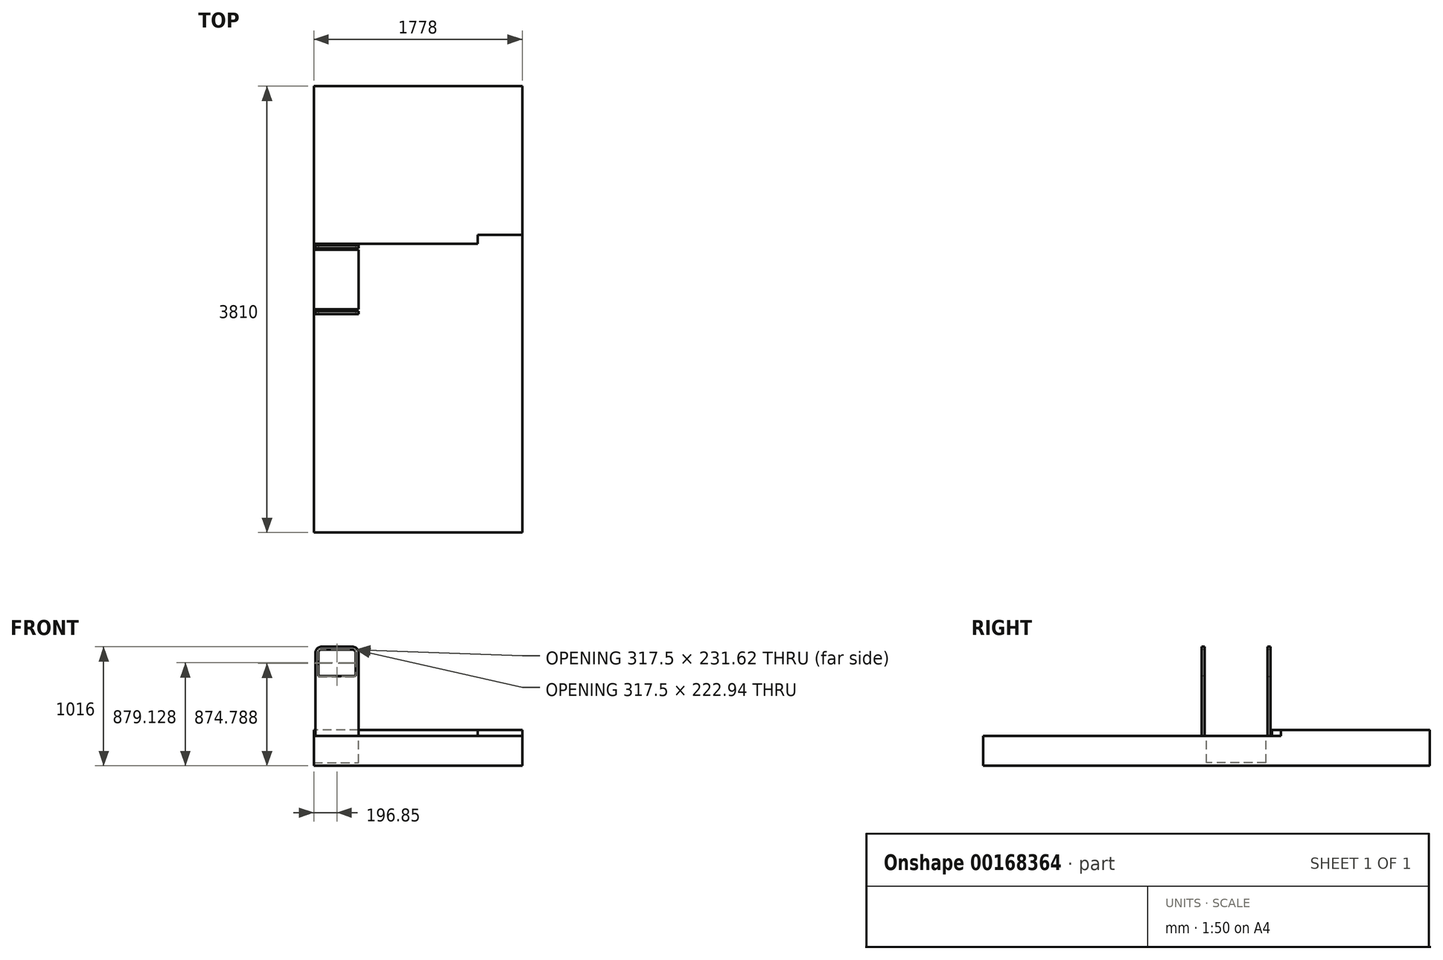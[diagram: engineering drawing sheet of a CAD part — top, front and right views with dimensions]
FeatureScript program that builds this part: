
annotation { "Feature Type Name" : "Feature", "Feature Type Description" : "" }
export const myFeature = defineFeature(function(context is Context, id is Id, definition is map)
    precondition{}
    {
        {
            var Q0;
            Q0=qCreatedBy(makeId("Top.planeOp"),FACE);
            var sketch = newSketch(context, id + "F0", { "sketchPlane" : qUnion([Q0])});
            skLineSegment(sketch, "E0.bottom", {"start": v(-889, 1905) * mm, "end": v(889, 1905) * mm});
            skLineSegment(sketch, "E0.top", {"start": v(-889, -1905) * mm, "end": v(889, -1905) * mm});
            skLineSegment(sketch, "E0.left", {"start": v(-889, 1905) * mm, "end": v(-889, -1905) * mm});
            skLineSegment(sketch, "E0.right", {"start": v(889, 1905) * mm, "end": v(889, -1905) * mm});
            skPoint(sketch, "E0.middle", {"position": v(0, 0) * mm});
            skLineSegment(sketch, "E1", {"start": v(889, 635) * mm, "end": v(508, 635) * mm});
            skLineSegment(sketch, "E2", {"start": v(508, 635) * mm, "end": v(508, 558.8) * mm});
            skLineSegment(sketch, "E3", {"start": v(508, 558.8) * mm, "end": v(-889, 558.8) * mm});
            skLineSegment(sketch, "E4", {"start": v(-889, 304.8) * mm, "end": v(-508, 304.8) * mm});
            skLineSegment(sketch, "E5", {"start": v(-508, 304.8) * mm, "end": v(-508, -304.8) * mm});
            skLineSegment(sketch, "E6", {"start": v(-508, -304.8) * mm, "end": v(-889, -304.8) * mm});
            skSolve(sketch);
        }
        {
            var Q0;
            {var subQ2=sQuery(id+"F0.wireOp",EDGE,"E0.bottom");Q0=makeQuery(id+"F0.imprint","IMPRINT",FACE,{"disambiguationData":[TD([[makeQuery(id+"F0.imprint","IMPRINT",EDGE,{"derivedFrom":subQ2}),-1.0]])]});}
            extrude(context, id + "F1", {"entities" : qUnion([Q0]), "depth" : 50.8 * mm});
        }
        {
            var Q0;
            Q0 = qSketchRegion(id + "F0", true);
            extrude(context, id + "F2", {"entities" : qUnion([Q0]), "operationType" : NewBodyOperationType.ADD, "oppositeDirection" : true, "depth" : 254 * mm});
        }
        {
            var Q0;
            Q0=makeQuery(id+"F2.opExtrude","CAP_FACE",FACE,{"disambiguationData":[OSD([sQuery(id+"F0.wireOp",EDGE,"E0.bottom"),sQuery(id+"F0.wireOp",EDGE,"E0.top"),sQuery(id+"F0.wireOp",EDGE,"E0.left"),sQuery(id+"F0.wireOp",EDGE,"E0.right")])],"isStart":true});
            var sketch = newSketch(context, id + "F3", { "sketchPlane" : qUnion([Q0])});
            skLineSegment(sketch, "E7", {"start": v(-889, 508) * mm, "end": v(-508, 508) * mm});
            skLineSegment(sketch, "E8", {"start": v(-508, 508) * mm, "end": v(-508, 0) * mm});
            skLineSegment(sketch, "E9", {"start": v(-508, 0) * mm, "end": v(-889, 0) * mm});
            skLineSegment(sketch, "E10", {"start": v(-889, 508) * mm, "end": v(-889, 0) * mm});
            skSolve(sketch);
        }
        {
            var Q0;
            Q0=makeQuery(id+"F3.imprint","IMPRINT",FACE,{"disambiguationData":[TD([[makeQuery(id+"F3.imprint","IMPRINT",EDGE,{"derivedFrom":sQuery(id+"F3.wireOp",EDGE,"E7")}),-1.0]])]});
            extrude(context, id + "F4", {"entities" : qUnion([Q0]), "operationType" : NewBodyOperationType.REMOVE, "oppositeDirection" : true, "depth" : 228.6 * mm});
        }
        {
            var Q0;
            Q0=makeQuery(id+"F2.opExtrude","CAP_FACE",FACE,{"disambiguationData":[OSD([sQuery(id+"F0.wireOp",EDGE,"E0.bottom"),sQuery(id+"F0.wireOp",EDGE,"E0.top"),sQuery(id+"F0.wireOp",EDGE,"E0.left"),sQuery(id+"F0.wireOp",EDGE,"E0.right")])],"isStart":true});
            var sketch = newSketch(context, id + "F5", { "sketchPlane" : qUnion([Q0])});
            skLineSegment(sketch, "E11", {"start": v(-2443.02, 548.85) * mm, "end": v(-2443.02, 2474.47) * mm});
            skLineSegment(sketch, "E12", {"start": v(-508, 522.13) * mm, "end": v(-508, 547.53) * mm});
            skLineSegment(sketch, "E13", {"start": v(-508, 547.53) * mm, "end": v(-876.3, 547.53) * mm});
            skLineSegment(sketch, "E14", {"start": v(-876.3, 547.53) * mm, "end": v(-876.3, 522.13) * mm});
            skLineSegment(sketch, "E15", {"start": v(-876.3, 522.13) * mm, "end": v(-508, 522.13) * mm});
            skSolve(sketch);
        }
        {
            var Q0;
            Q0=makeQuery(id+"F5.imprint","IMPRINT",FACE,{"disambiguationData":[TD([[makeQuery(id+"F5.imprint","IMPRINT",EDGE,{"derivedFrom":sQuery(id+"F5.wireOp",EDGE,"E12")}),1.0]])]});
            extrude(context, id + "F6", {"entities" : qUnion([Q0]), "operationType" : NewBodyOperationType.ADD, "depth" : 762 * mm});
        }
        {
            var Q0;
            Q0=makeQuery(id+"F6.opExtrude","CAP_EDGE",EDGE,{"disambiguationData":[OSD([sQuery(id+"F5.wireOp",EDGE,"E14")])],"isStart":false});
            fillet(context, id + "F7", {"entities" : qUnion([Q0]), "radius" : 50.8 * mm, "tangentPropagation" : true, "allowEdgeOverflow" : false});
        }
        {
            var Q0;
            Q0=makeQuery(id+"F6.opExtrude","CAP_EDGE",EDGE,{"disambiguationData":[OSD([sQuery(id+"F5.wireOp",EDGE,"E12")])],"isStart":false});
            fillet(context, id + "F8", {"entities" : qUnion([Q0]), "radius" : 50.8 * mm, "tangentPropagation" : true, "allowEdgeOverflow" : false});
        }
        {
            var Q0;
            Q0=makeQuery(id+"F6.opExtrude","SWEPT_FACE",FACE,{"disambiguationData":[OSD([sQuery(id+"F5.wireOp",EDGE,"E15")])]});
            var sketch = newSketch(context, id + "F9", { "sketchPlane" : qUnion([Q0])});
            skLineSegment(sketch, "E16", {"start": v(-850.9, 504.98) * mm, "end": v(-533.4, 504.98) * mm});
            skLineSegment(sketch, "E17", {"start": v(-533.4, 504.98) * mm, "end": v(-533.4, 711.2) * mm});
            skLineSegment(sketch, "E18", {"start": v(-558.8, 736.6) * mm, "end": v(-825.5, 736.6) * mm});
            skLineSegment(sketch, "E19", {"start": v(-850.9, 711.2) * mm, "end": v(-850.9, 504.98) * mm});
            skPoint(sketch, "E20.visualSharp", {"position": v(-850.9, 736.6) * mm});
            skArc(sketch, "E20.filletArc", {"start": v(-825.5, 736.6) * mm, "mid": v(-843.46, 729.16) * mm, "end": v(-850.9, 711.2) * mm});
            skPoint(sketch, "E21.visualSharp", {"position": v(-533.4, 736.6) * mm});
            skArc(sketch, "E21.filletArc", {"start": v(-533.4, 711.2) * mm, "mid": v(-540.84, 729.16) * mm, "end": v(-558.8, 736.6) * mm});
            skSolve(sketch);
        }
        {
            var Q0;
            Q0=makeQuery(id+"F9.imprint","IMPRINT",FACE,{"disambiguationData":[TD([[makeQuery(id+"F9.imprint","IMPRINT",EDGE,{"derivedFrom":sQuery(id+"F9.wireOp",EDGE,"E16")}),1.0]])]});
            extrude(context, id + "F10", {"entities" : qUnion([Q0]), "operationType" : NewBodyOperationType.REMOVE, "oppositeDirection" : true, "depth" : 25.4 * mm});
        }
        {
            var Q0;
            Q0=makeQuery(id+"F2.opExtrude","CAP_FACE",FACE,{"disambiguationData":[OSD([sQuery(id+"F0.wireOp",EDGE,"E0.bottom"),sQuery(id+"F0.wireOp",EDGE,"E0.top"),sQuery(id+"F0.wireOp",EDGE,"E0.left"),sQuery(id+"F0.wireOp",EDGE,"E0.right")])],"isStart":true});
            var sketch = newSketch(context, id + "F11", { "sketchPlane" : qUnion([Q0])});
            skLineSegment(sketch, "E22", {"start": v(-876.3, -15.7) * mm, "end": v(-508, -15.7) * mm});
            skLineSegment(sketch, "E23", {"start": v(-508, -15.7) * mm, "end": v(-508, -41.1) * mm});
            skLineSegment(sketch, "E24", {"start": v(-508, -41.1) * mm, "end": v(-876.3, -41.1) * mm});
            skLineSegment(sketch, "E25", {"start": v(-876.3, -41.1) * mm, "end": v(-876.3, -15.7) * mm});
            skSolve(sketch);
        }
        {
            var Q0;
            Q0=makeQuery(id+"F11.imprint","IMPRINT",FACE,{"disambiguationData":[TD([[makeQuery(id+"F11.imprint","IMPRINT",EDGE,{"derivedFrom":sQuery(id+"F11.wireOp",EDGE,"E22")}),-1.0]])]});
            extrude(context, id + "F12", {"entities" : qUnion([Q0]), "operationType" : NewBodyOperationType.ADD, "depth" : 762 * mm});
        }
        {
            var Q0;
            Q0=makeQuery(id+"F12.opExtrude","CAP_EDGE",EDGE,{"disambiguationData":[OSD([sQuery(id+"F11.wireOp",EDGE,"E25")])],"isStart":false});
            fillet(context, id + "F13", {"entities" : qUnion([Q0]), "radius" : 50.8 * mm, "tangentPropagation" : true, "allowEdgeOverflow" : false});
        }
        {
            var Q0;
            Q0=makeQuery(id+"F12.opExtrude","CAP_EDGE",EDGE,{"disambiguationData":[OSD([sQuery(id+"F11.wireOp",EDGE,"E23")])],"isStart":false});
            fillet(context, id + "F14", {"entities" : qUnion([Q0]), "radius" : 50.8 * mm, "tangentPropagation" : true, "allowEdgeOverflow" : false});
        }
        {
            var Q0;
            Q0=makeQuery(id+"F12.opExtrude","SWEPT_FACE",FACE,{"disambiguationData":[OSD([sQuery(id+"F11.wireOp",EDGE,"E24")])]});
            var sketch = newSketch(context, id + "F15", { "sketchPlane" : qUnion([Q0])});
            skLineSegment(sketch, "E26", {"start": v(-850.9, 513.66) * mm, "end": v(-533.4, 513.66) * mm});
            skLineSegment(sketch, "E27", {"start": v(-533.4, 513.66) * mm, "end": v(-533.4, 711.2) * mm});
            skLineSegment(sketch, "E28", {"start": v(-558.8, 736.6) * mm, "end": v(-825.5, 736.6) * mm});
            skLineSegment(sketch, "E29", {"start": v(-850.9, 711.2) * mm, "end": v(-850.9, 513.66) * mm});
            skPoint(sketch, "E30.visualSharp", {"position": v(-850.9, 736.6) * mm});
            skArc(sketch, "E30.filletArc", {"start": v(-825.5, 736.6) * mm, "mid": v(-843.46, 729.16) * mm, "end": v(-850.9, 711.2) * mm});
            skPoint(sketch, "E31.visualSharp", {"position": v(-533.4, 736.6) * mm});
            skArc(sketch, "E31.filletArc", {"start": v(-533.4, 711.2) * mm, "mid": v(-540.84, 729.16) * mm, "end": v(-558.8, 736.6) * mm});
            skSolve(sketch);
        }
        {
            var Q0;
            Q0=makeQuery(id+"F15.imprint","IMPRINT",FACE,{"disambiguationData":[TD([[makeQuery(id+"F15.imprint","IMPRINT",EDGE,{"derivedFrom":sQuery(id+"F15.wireOp",EDGE,"E26")}),1.0]])]});
            extrude(context, id + "F16", {"entities" : qUnion([Q0]), "operationType" : NewBodyOperationType.REMOVE, "oppositeDirection" : true, "depth" : 25.4 * mm});
        }
    });
